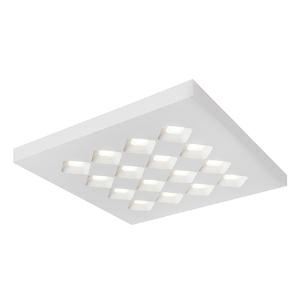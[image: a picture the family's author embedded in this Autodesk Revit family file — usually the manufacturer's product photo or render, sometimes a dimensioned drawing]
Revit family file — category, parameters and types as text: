
# Revit family: 3f_filippi_-_3f_diagon_p_soft_ugr_3f_filippi_-_12126_-_3f_diagon_p_25w-830_soft_ugr_596x596
name_source: partatom
category: Lighting Fixtures
units: mm (PartAtom-declared; Revit-internal decimal feet)

## family parameters
Cut with Voids When Loaded = No
Host = Face
Light Source = No
Part Type = Normal
Room Calculation Point = No
Round Connector Dimension = Use Diameter
Shared = No

## types (1)
- 3F Filippi - 3F Dìagon P Soft UGR (1 x LED, 3495 lm, 28 W, 3000 K)
    Apparent Load = 28 VA
    Approval mark = CE
    CIE Flux Codes = 59 92 100 100 100
    Color Rendering = 80
    Color Temperature = 3000 K
    Control Gear = Electronic ballast
    Default Elevation = 1800 mm
    Description = ILLUMINOTECHNICAL
Luminous efficiency 100% (DLOR 100%, ULOR 0%).
Initial luminous flux of the luminaire 3495 lm.
Direct symmetric distribution.
Installation Interdistance Transv.D = 1.23 x hu - Long.D = 1.23 x hu.
Average luminance <3000 cd/m² for radial angles >65°.
Tabular UGR (CIE 117 - 4H-8H; S=0.25H; 70/50/20): RUG 18.6 - 18.5.
Beam angle: 102° - 101°.
Luminous efficacy 125 lm/W.
Lifetime (L95/B10): 30000 h. (tq+25°C)
Lifetime (L90/B10): 50000 h. (tq+25°C)
Lifetime (L80/B10): 80000 h. (tq+25°C)
Lifetime (L75/B10): 100000 h. (tq+25°C)
Sudden decreased luminous flux after 50000 hours: 0% (C0).
Photobiological safety in compliance with IEC/TR 62778: RG0 risk exempt, (IEC 62471).
In compliance with IEC/EN 62722-2-1 - IEC/EN 62717 standards.

SOURCE
Squared LED module 25W/830.
Energy efficiency class (UE 2019/2020 - UE 2019/2015): C.
CIE 13.3 Colour rendering index: CRI >80 (R9 <50%).
IES TM-30 Fidelity Index: Rf = 84 Rg = 95.
CCT nominal colour temperature 3000 K.
Colour initial tolerance (MacAdam): SDCM 3.

MECHANICAL
White painted frame.
Height only 40 mm.
Housing in hot-galvanised steel, painted in white polyester.
Honeycombed diagonal screen in white anti-glare polycarbonate.
Opal methacrylate (PMMA) rhomboid lenses with differentiated, engraved and prismatic surfaces for diffused, soft lighting and excellent visual comfort.
Luminaire with limited surface temperature. - D - (EN 60598-2-24)
Dimensions: 596x596 mm, height 40 mm. Weight 6.175 kg.
IP40 protection degree.
Mechanical strength to impacts IK06 (1 joule).
Glow-wire test resistance 650°C.

ELECTRICAL
Halogen Free electronic wiring 230V-50/60Hz, power factor 0.95, THD <25%, constant output current, class I, 1 driver.
Power of the luminaire 28 W.
ENEC - CE.
SAFE FLICKER: PstLM=<1 and SVM=<0.4 (IEC TR 61547-1 and IEC TR 63158), to ensure a more comfortable and safe light.
Luminaire compliant with EN 60598-2-22 for power supply from a centralised emergency system CPSS (Central Power Supply System), not incorporated in the luminaire - high risk areas excluded. The default power and flux are 100% in AC and 100% in DC.
Ambient temperature from 0°C to +25°C.
Temperature class T6 max 85°C.
Quick connection.
Relative humidity UR: <85%.

INSTALLATION
Ceiling.

APPLICATIONS
Environments: staterooms, with VDTs, offices.
Environments with exacting visual tasks, where diffused soft light for optimum visual comfort is required.

WARNING
Luminaire designed for disposal/recycling at end-of-life.
Replaceable (LED only) light source by a professional. Replaceable control gear by a professional.
    Height = 40 mm  [stored 0.131234 ft]
    Lamp = 1 x LED
    Lamp Light Flux = 3495 lm
    Lamp Power = 28 W
    Lamp count = 1
    Length = 596 mm
    Lifetime = 50000 h
    Luminous efficacy = 125 lm/W
    Manufacturer = 3F Filippi
    ModVariant = No
    Model = 3F Filippi - 12126 - 3F Diagon P 25W-830 SOFT UGR 596x596
    Mounting Place = Ceiling
    Mounting Type = Surface mounted
    Number of Poles = 1
    OnlyDefault = Yes
    Power Factor = 1
    Product Name = 3F Filippi - 3F Dìagon P Soft UGR
    Product group = ceiling mounted luminaire
    ProductGroupID = 3
    Protection Class = Protection class I
    Protection Degree = IP 40
    RLX_Detail_Level = 1
    RLX_Emergency_Light_Flux = 0 lm
    RLX_Emergency_Type = 0
    RLX_Emergency_Type_DB = No
    RlxData = <blob elided: 94957 chars, md5=52b146a8>
    Socket = socket
    Standby Power = 0 W
    System Light Flux = 3495 lm
    System Power = 28 W
    Type Comments = Product without accessories
    Type Image = 3ffilippi_3f_diagon_p_soft_ugr.jpg
    URL = http://relux.com
    VarID = ---
    Voltage = 0 V
    Weight = 0.00 kg
    Width = 596 mm

note: [stored X ft] marks values corroborated as IEEE doubles in the binary element streams (Revit-internal decimal feet)

## geometry (parser evidence)
native form markers: Blend x4, Sweep x10
no freeform markers — native parametric forms only
